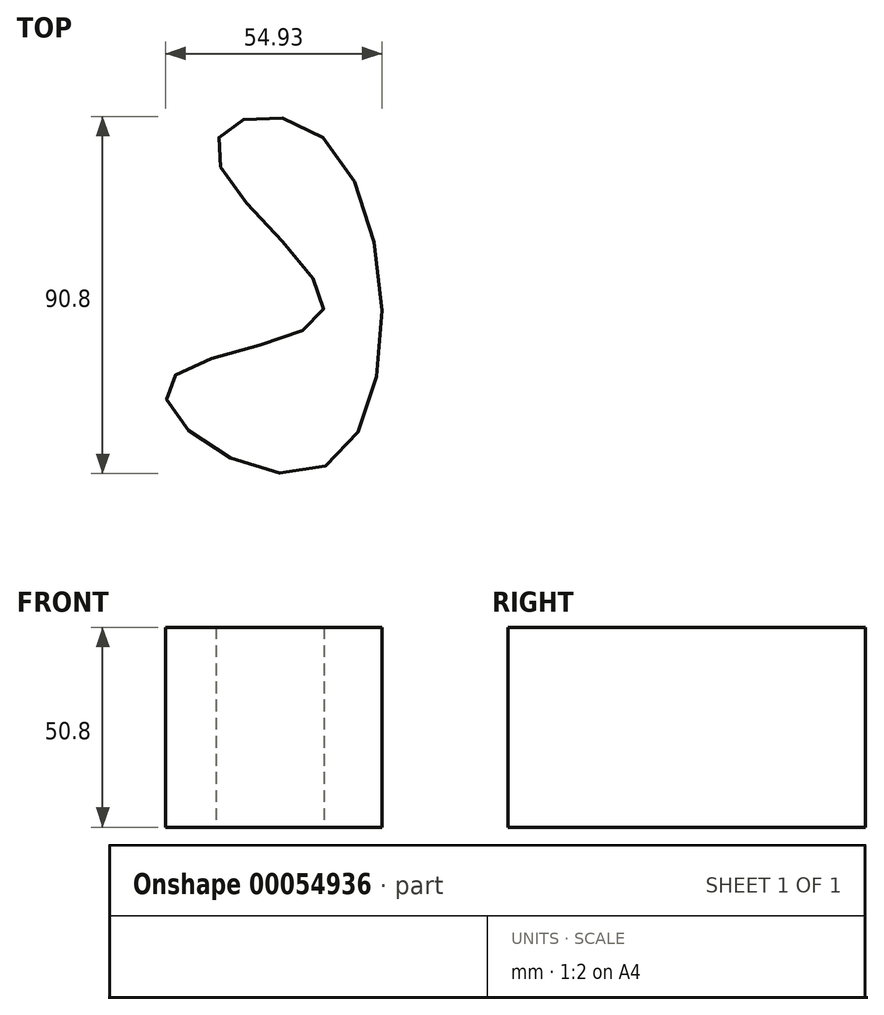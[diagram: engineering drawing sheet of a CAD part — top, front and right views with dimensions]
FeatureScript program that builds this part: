
annotation { "Feature Type Name" : "Feature", "Feature Type Description" : "" }
export const myFeature = defineFeature(function(context is Context, id is Id, definition is map)
    precondition{}
    {
        {
            var Q0;
            Q0=qCreatedBy(makeId("Top.planeOp"),FACE);
            var sketch = newSketch(context, id + "F1", { "sketchPlane" : qUnion([Q0])});
            skFitSpline(sketch, "E0", {"points": [v(0, 44.27) * mm, v(-27.17, 41.14) * mm, v(0, 0) * mm, v(-39.66, -18.87) * mm, v(0, -39.5) * mm, v(0, 44.27) * mm]});
            skSolve(sketch);
        }
        {
            var Q0;
            Q0 = qSketchRegion(id + "F1", true);
            extrude(context, id + "F0", {"entities" : qUnion([Q0]), "depth" : 50.8 * mm});
        }
    });
